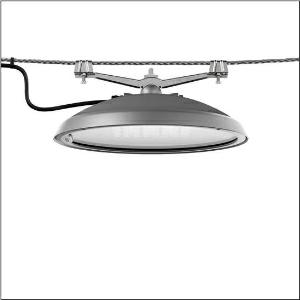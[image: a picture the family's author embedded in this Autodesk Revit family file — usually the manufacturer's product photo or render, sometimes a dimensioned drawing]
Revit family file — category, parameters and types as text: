
# Revit family: dl_r__50_iq_mini___p1_0s_5xa248u41f08ge_754b
name_source: partatom
category: Lighting Fixtures
units: mm (PartAtom-declared; Revit-internal decimal feet)

## family parameters
Cut with Voids When Loaded = No
Host = Face
Light Source = No
Part Type = Normal
Room Calculation Point = No
Round Connector Dimension = Use Diameter
Shared = No

## types (1)
- --- (1 x LED, 5030 lm, 31.2 W, 4000K)
    Apparent Load = 31 VA
    CIE Flux Codes = 23 54 93 100 100
    Color Rendering = 70
    Color Temperature = 4000K
    Default Elevation = 1800 mm
    Description = DL® 50 iQ mini, catenary luminaire, primary light control with lens, of PMMA, primary optical cover: cover, of toughened safety glass, transparent, light distribution: P1.0s, light emission: direct distribution, primary light characteristic: symmetric, installation type: suspended mounting, LED, High Power LED, rated luminous flux: 5.030lm, luminous efficacy: 161lm/W, light colour: 740, colour temperature: 4000K, control: optimised constant luminous flux control (CLO 2.0), Desk-Remote (wireless, voltage-free reading and setting of iQ features in the workshop via application-optimized NFC function/RFID function), Light-Fading, Smart-Wire, Night-Set, Lumen-Switch, Temp-Guard, Auto-Match, Street-Remote, mains connection: 230..240V, AC, 50/60Hz, start of lifetime: 31W, end of service life: 32W, reduction: 15W, luminaire housing, of diecast aluminium, powder-coated, Siteco® metallic grey (DB 702S), diameter: 500mm, height: 115mm, protection rating (complete): IP66, insulation class (complete): insulation class II (safety insulation), certification: CE, ENEC, VDE, impact resistance: IK08, permissible operating ambient temperature for outdoor applications: -25..+40°C, standard-compliant lighting for roads and squares, packaging unit: 1 piece

Light Distribution: P1.0s
    Height = 124 mm  [stored 0.406824 ft]
    Lamp = 1 x LED
    Lamp Light Flux = 5030 lm
    Lamp Power = 31.2 W
    Lamp count = 1
    Length = 500 mm
    Luminous efficacy = 161 lm/W
    Manufacturer = Siteco
    ModVariant = No
    Model = 5XA248U41F08GE
    Number of Poles = 1
    OnlyDefault = Yes
    Power Factor = 1
    Product Name = DL® 50 iQ mini | P1.0s
    Product group = catenary luminaire
    ProductGroupID = 6300
    Protection Class = Protection class II
    Protection Degree = IP 66
    RLX_Detail_Level = 1
    RLX_Emergency_Light_Flux = 0 lm
    RLX_Emergency_Type = 0
    RLX_Emergency_Type_DB = No
    RlxData = <blob elided: 123673 chars, md5=18ddefbb>
    Socket = socket
    Standby Power = 0 W
    System Light Flux = 5030 lm
    System Power = 31 W
    Type Comments = factory setting: luminous flux: 100 % | dim-lin: 254 | 325 mA
    Type Image = l_1242791.jpg
    URL = http://relux.com
    VarID = @adj_071509
    Voltage = 0 V
    Weight = 0.00 kg
    Width = 0 mm  [stored 0 ft]

note: [stored X ft] marks values corroborated as IEEE doubles in the binary element streams (Revit-internal decimal feet)

## geometry (parser evidence)
native form markers: Blend x4, Sweep x13
no freeform markers — native parametric forms only
